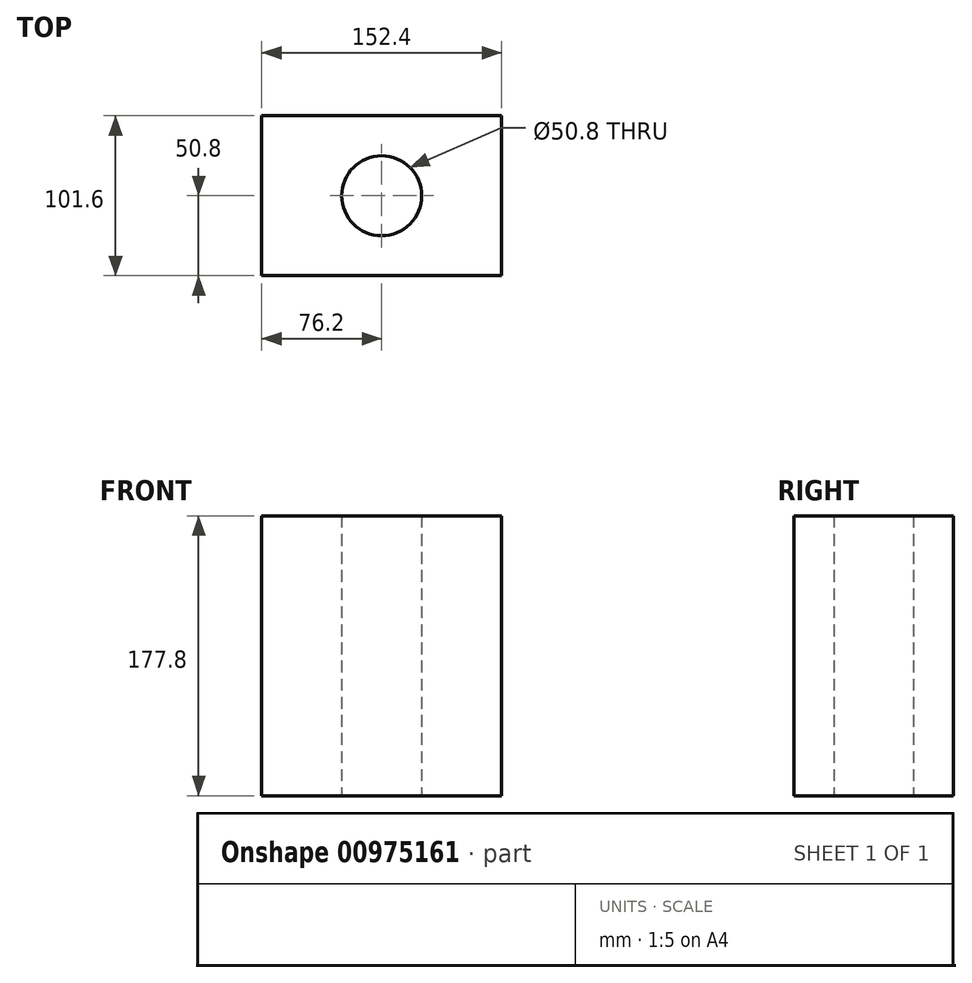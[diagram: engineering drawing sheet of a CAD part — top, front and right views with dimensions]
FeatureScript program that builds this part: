
annotation { "Feature Type Name" : "Feature", "Feature Type Description" : "" }
export const myFeature = defineFeature(function(context is Context, id is Id, definition is map)
    precondition{}
    {
        {
            var Q0;
            Q0=qCreatedBy(makeId("Top.planeOp"),FACE);
            var sketch = newSketch(context, id + "F0", { "sketchPlane" : qUnion([Q0])});
            skLineSegment(sketch, "E0.bottom", {"start": v(-76.2, 50.8) * mm, "end": v(76.2, 50.8) * mm});
            skLineSegment(sketch, "E0.top", {"start": v(-76.2, -50.8) * mm, "end": v(76.2, -50.8) * mm});
            skLineSegment(sketch, "E0.left", {"start": v(-76.2, 50.8) * mm, "end": v(-76.2, -50.8) * mm});
            skLineSegment(sketch, "E0.right", {"start": v(76.2, 50.8) * mm, "end": v(76.2, -50.8) * mm});
            skPoint(sketch, "E0.middle", {"position": v(0, 0) * mm});
            skSolve(sketch);
        }
        {
            var Q0;
            Q0=makeQuery(id+"F0.imprint","IMPRINT",FACE,{"disambiguationData":[TD([[makeQuery(id+"F0.imprint","IMPRINT",EDGE,{"derivedFrom":sQuery(id+"F0.wireOp",EDGE,"E0.bottom")}),-1.0]])]});
            var sketch = newSketch(context, id + "F1", { "sketchPlane" : qUnion([Q0])});
            skCircle(sketch, "E1", {"center": v(0, 0) * mm, "radius": 25.4 * mm});
            skSolve(sketch);
        }
        {
            var Q0;
            Q0=makeQuery(id+"F1.imprint","IMPRINT",FACE,{"disambiguationData":[TD([[makeQuery(id+"F1.imprint","IMPRINT",EDGE,{"derivedFrom":sQuery(id+"F1.wireOp",EDGE,"E1")}),-1.0]])]});
            extrude(context, id + "F2", {"entities" : qUnion([Q0]), "depth" : 177.8 * mm, "offsetDistance" : 25.4 * mm});
        }
    });
